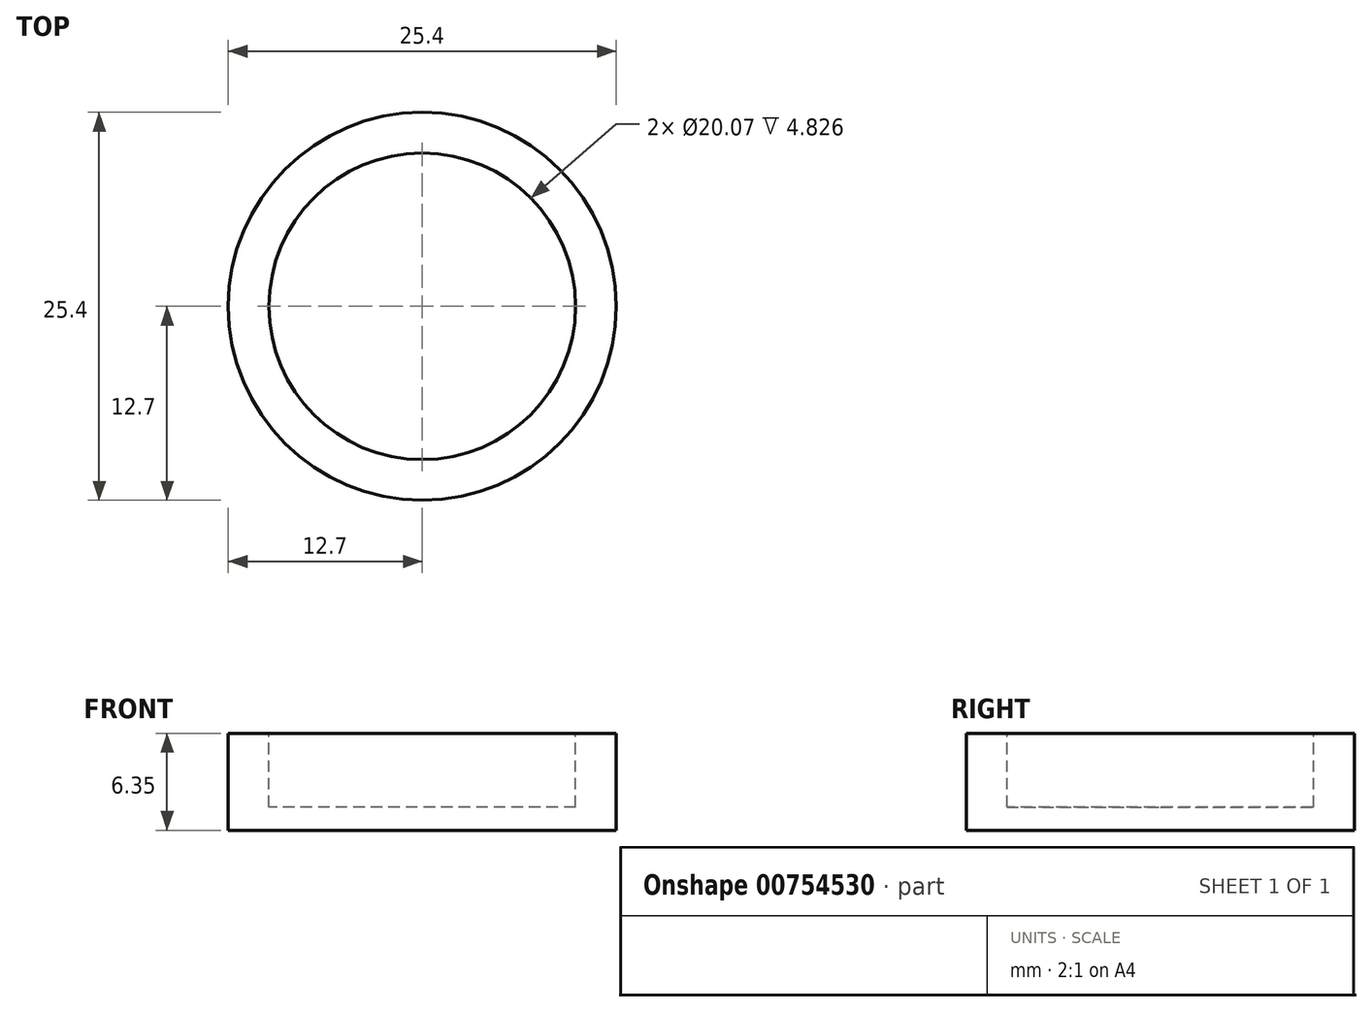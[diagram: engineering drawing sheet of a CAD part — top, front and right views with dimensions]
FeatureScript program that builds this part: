
annotation { "Feature Type Name" : "Feature", "Feature Type Description" : "" }
export const myFeature = defineFeature(function(context is Context, id is Id, definition is map)
    precondition{}
    {
        {
            var Q0;
            Q0=qCreatedBy(makeId("Top.planeOp"),FACE);
            var sketch = newSketch(context, id + "F0", { "sketchPlane" : qUnion([Q0])});
            skCircle(sketch, "E0", {"center": v(0, 0) * mm, "radius": 12.7 * mm});
            skSolve(sketch);
        }
        {
            var Q0;
            Q0=makeQuery(id+"F0.imprint","IMPRINT",FACE,{"disambiguationData":[TD([[makeQuery(id+"F0.imprint","IMPRINT",EDGE,{"derivedFrom":sQuery(id+"F0.wireOp",EDGE,"E0")}),1.0]])]});
            extrude(context, id + "F1", {"entities" : qUnion([Q0]), "oppositeDirection" : true, "depth" : 6.35 * mm, "offsetDistance" : 25.4 * mm});
        }
        {
            var Q0;
            Q0=makeQuery(id+"F1.opExtrude","CAP_FACE",FACE,{"disambiguationData":[OSD([sQuery(id+"F0.wireOp",EDGE,"E0")])],"isStart":true});
            var sketch = newSketch(context, id + "F2", { "sketchPlane" : qUnion([Q0])});
            skCircle(sketch, "E1", {"center": v(0, 0) * mm, "radius": 10.03 * mm});
            skSolve(sketch);
        }
        {
            var Q0;
            Q0 = qSketchRegion(id + "F2", true);
            extrude(context, id + "F3", {"entities" : qUnion([Q0]), "operationType" : NewBodyOperationType.REMOVE, "oppositeDirection" : true, "depth" : 4.83 * mm, "offsetDistance" : 25.4 * mm});
        }
    });
